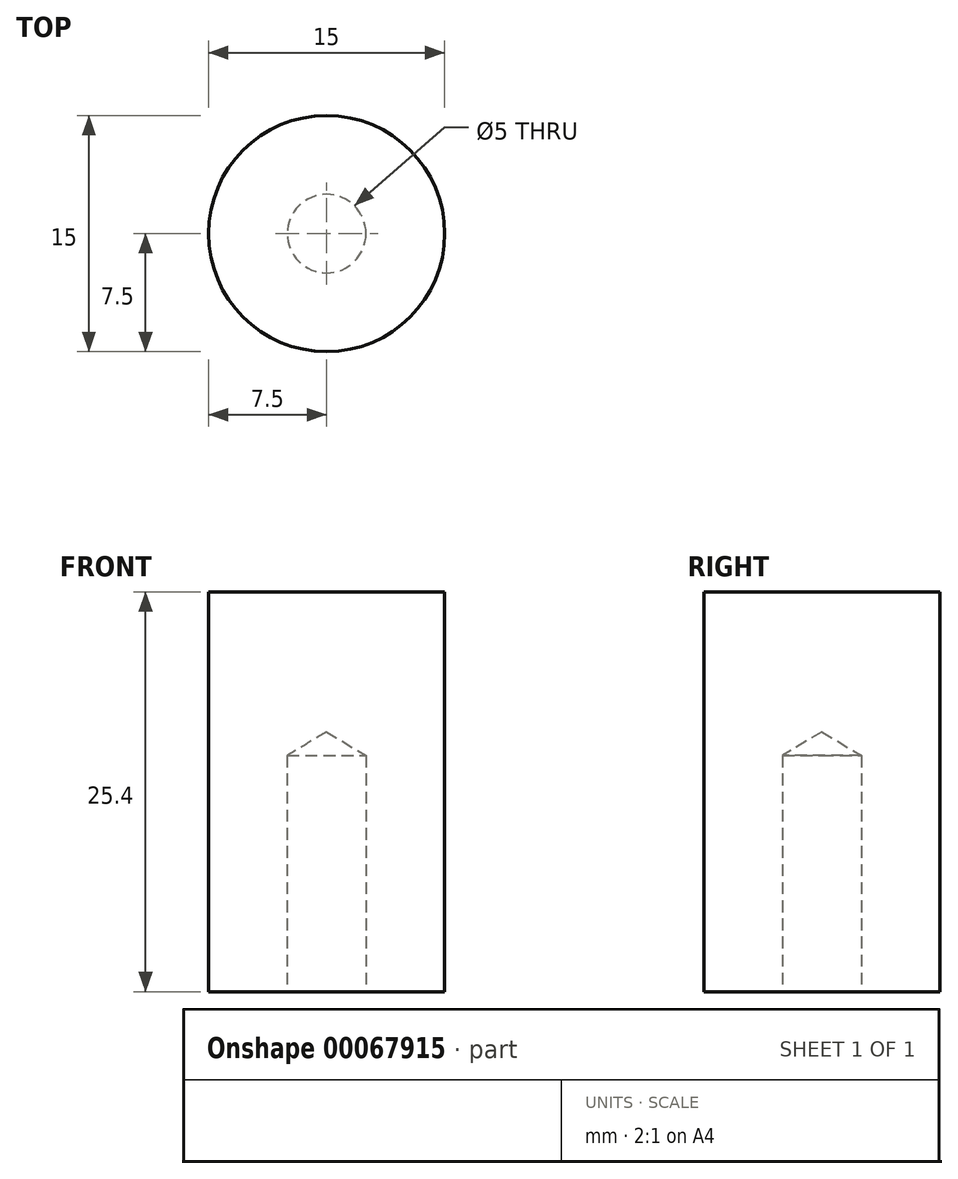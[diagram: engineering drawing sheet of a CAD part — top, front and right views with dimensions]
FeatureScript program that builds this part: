
annotation { "Feature Type Name" : "Feature", "Feature Type Description" : "" }
export const myFeature = defineFeature(function(context is Context, id is Id, definition is map)
    precondition{}
    {
        {
            var Q0;
            Q0=qCreatedBy(makeId("Top.planeOp"),FACE);
            var sketch = newSketch(context, id + "F0", { "sketchPlane" : qUnion([Q0])});
            skCircle(sketch, "E0", {"center": v(0, 0) * mm, "radius": 7.5 * mm});
            skSolve(sketch);
        }
        {
            var Q0;
            Q0 = qSketchRegion(id + "F0", true);
            extrude(context, id + "F1", {"entities" : qUnion([Q0]), "depth" : 25.4 * mm});
        }
        {
            var Q0;
            Q0=sQuery(id+"F0.wireOp",VERTEX,"E0.center");
            var Q1;
            Q1=makeQuery(id+"F1.opExtrude","SWEPT_BODY",BODY,{"disambiguationData":[OSD([sQuery(id+"F0.wireOp",EDGE,"E0")])]});
            hole(context, id + "F2", {"style" : HoleStyle.SIMPLE, "endStyle" : HoleEndStyle.BLIND, "oppositeDirection" : true, "holeDiameter" : 5 * mm, "holeDepth" : 15 * mm, "locations" : qUnion([Q0]), "scope" : qUnion([Q1])});
        }
    });
